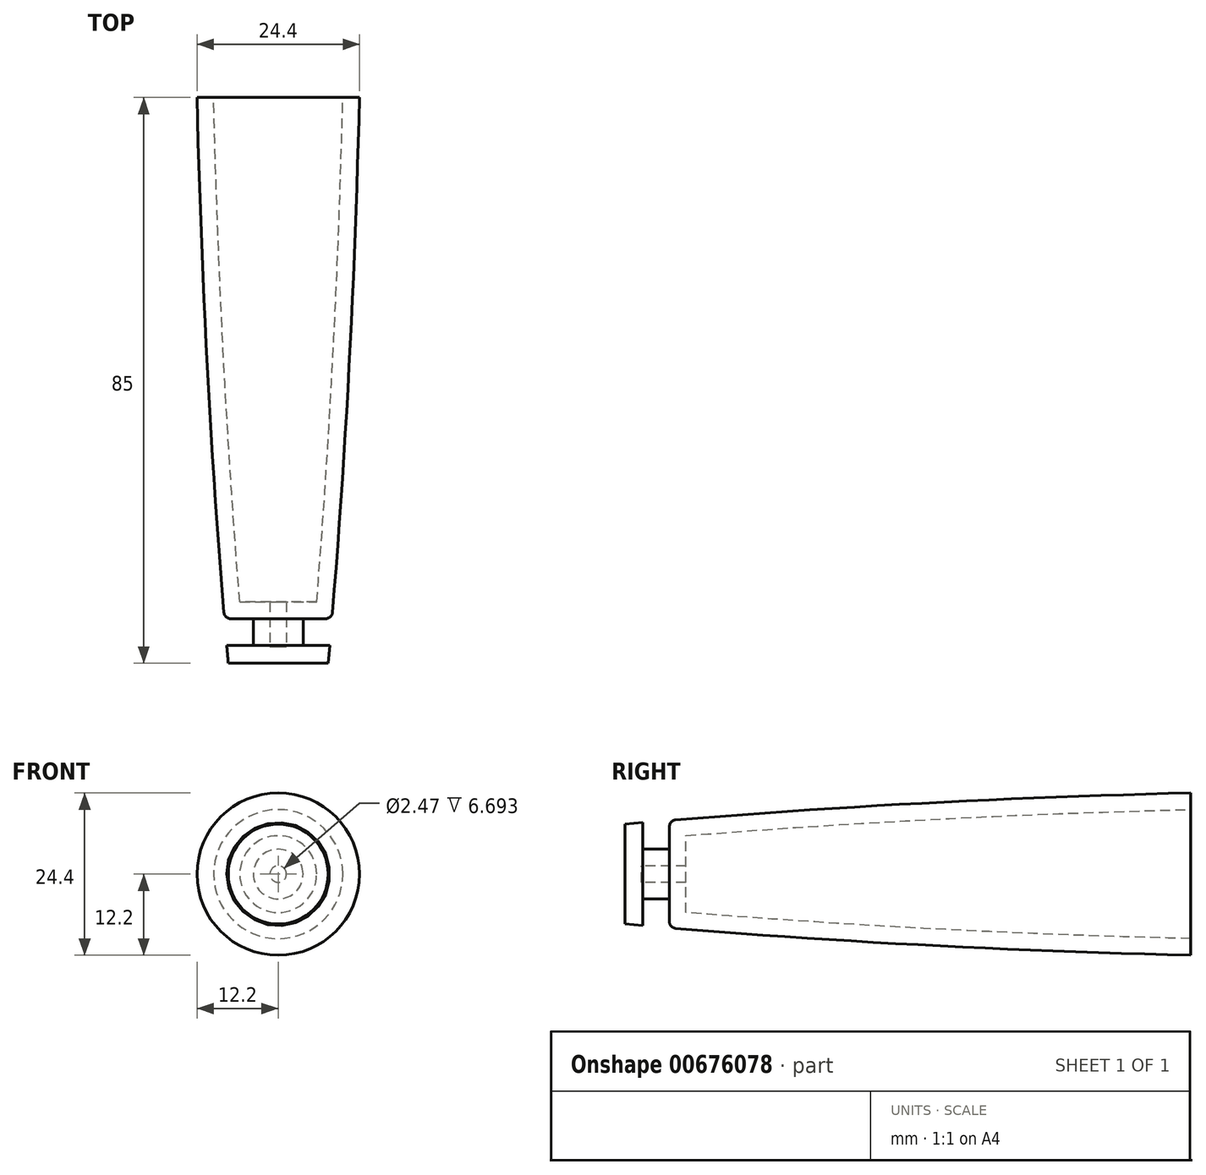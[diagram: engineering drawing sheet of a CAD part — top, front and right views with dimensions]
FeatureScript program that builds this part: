
annotation { "Feature Type Name" : "Feature", "Feature Type Description" : "" }
export const myFeature = defineFeature(function(context is Context, id is Id, definition is map)
    precondition{}
    {
        {
            var Q0;
            Q0=qCreatedBy(makeId("Top.planeOp"),FACE);
            var sketch = newSketch(context, id + "F0", { "sketchPlane" : qUnion([Q0])});
            skLineSegment(sketch, "E0", {"start": v(0, 0) * mm, "end": v(0, 42.5) * mm});
            skLineSegment(sketch, "E1", {"start": v(0, 0) * mm, "end": v(0, -42.5) * mm});
            skLineSegment(sketch, "E2", {"start": v(0, -42.5) * mm, "end": v(-7.5, -42.5) * mm});
            skLineSegment(sketch, "E3", {"start": v(0, 42.5) * mm, "end": v(-12.2, 42.5) * mm});
            skFitSpline(sketch, "E4", {"points": [v(-12.2, 42.5) * mm, v(-7.5, -42.5) * mm], "startDerivative": vector(2.15, -88.38) * mm, "endDerivative": vector(7.31, -82.7) * mm});
            skLineSegment(sketch, "E5", {"start": v(-7.5, -42.5) * mm, "end": v(-7.74, -39.8) * mm});
            skLineSegment(sketch, "E6", {"start": v(-7.74, -39.8) * mm, "end": v(-3.74, -39.8) * mm});
            skLineSegment(sketch, "E7", {"start": v(-3.74, -39.8) * mm, "end": v(-3.74, -35.8) * mm});
            skLineSegment(sketch, "E8", {"start": v(-3.74, -35.8) * mm, "end": v(-7.15, -35.8) * mm});
            skFitSpline(sketch, "E9.trimOffspring", {"points": [v(-12.2, 42.5) * mm, v(-7.5, -42.5) * mm], "startDerivative": vector(2.15, -88.38) * mm, "endDerivative": vector(7.31, -82.7) * mm});
            skPoint(sketch, "E10.visualSharp", {"position": v(-8.07, -35.8) * mm});
            skArc(sketch, "E10.filletArc", {"start": v(-8.15, -34.89) * mm, "mid": v(-7.83, -35.54) * mm, "end": v(-7.15, -35.8) * mm});
            skSolve(sketch);
        }
        {
            var Q0;
            Q0=makeQuery(id+"F0.imprint","IMPRINT",FACE,{"disambiguationData":[TD([[makeQuery(id+"F0.imprint","IMPRINT",EDGE,{"derivedFrom":sQuery(id+"F0.wireOp",EDGE,"E0")}),1.0]])]});
            var Q1;
            Q1=sQuery(id+"F0.wireOp",EDGE,"E0");
            revolve(context, id + "F1", {"entities" : qUnion([Q0]), "axis" : qUnion([Q1]), "revolveType" : RevolveType.FULL});
        }
        {
            var Q0;
            Q0=makeQuery(id+"F1.opRevolve","SWEPT_FACE",FACE,{"disambiguationData":[OSD([sQuery(id+"F0.wireOp",EDGE,"E3")])]});
            shell(context, id + "F2", {"entities" : qUnion([Q0]), "thickness" : 2.5 * mm});
        }
    });
